# Revit family: Medical_Furniture_Shield-Casework_Bedside-Cart
name_source: partatom
category: Furniture
units: mm (PartAtom-declared; Revit-internal decimal feet)

## family parameters
Always vertical = Yes
Cut with Voids When Loaded = No
OmniClass Number = 23.40.70.11.14.21
OmniClass Title = Health Care Furniture
Room Calculation Point = No
Shared = No
Work Plane-Based = No

## types (3) — shared parameters
Assembly Code = E20
Depth = 20 "
Description = Bedside Cart
Edition number = 1
Finish = Acrylic Solid Surface
Keynote = 12300
Manufacturer = Shield Casework
URL = https://www.shieldcasework.com
Width = 18 "
z_Continuous Tab Handle = Handle : Continuous Tab
z_Wire Pull Handle = Handle : Wire Pull
zero-valued in all types: Default Elevation

## per-type parameters (varying)
| type | z_One Drawer | z_Three Drawers | z_Two Drawers |
| Bedside Cart - One Drawer | Yes | No | No |
| Bedside Cart - Two Drawers | No | No | Yes |
| Bedside Cart - Three Drawers | No | Yes | No |

note: column(s) folded — value = type name in every type: Model

## geometry (parser evidence)
native form markers: Sweep x8
no freeform markers — native parametric forms only
